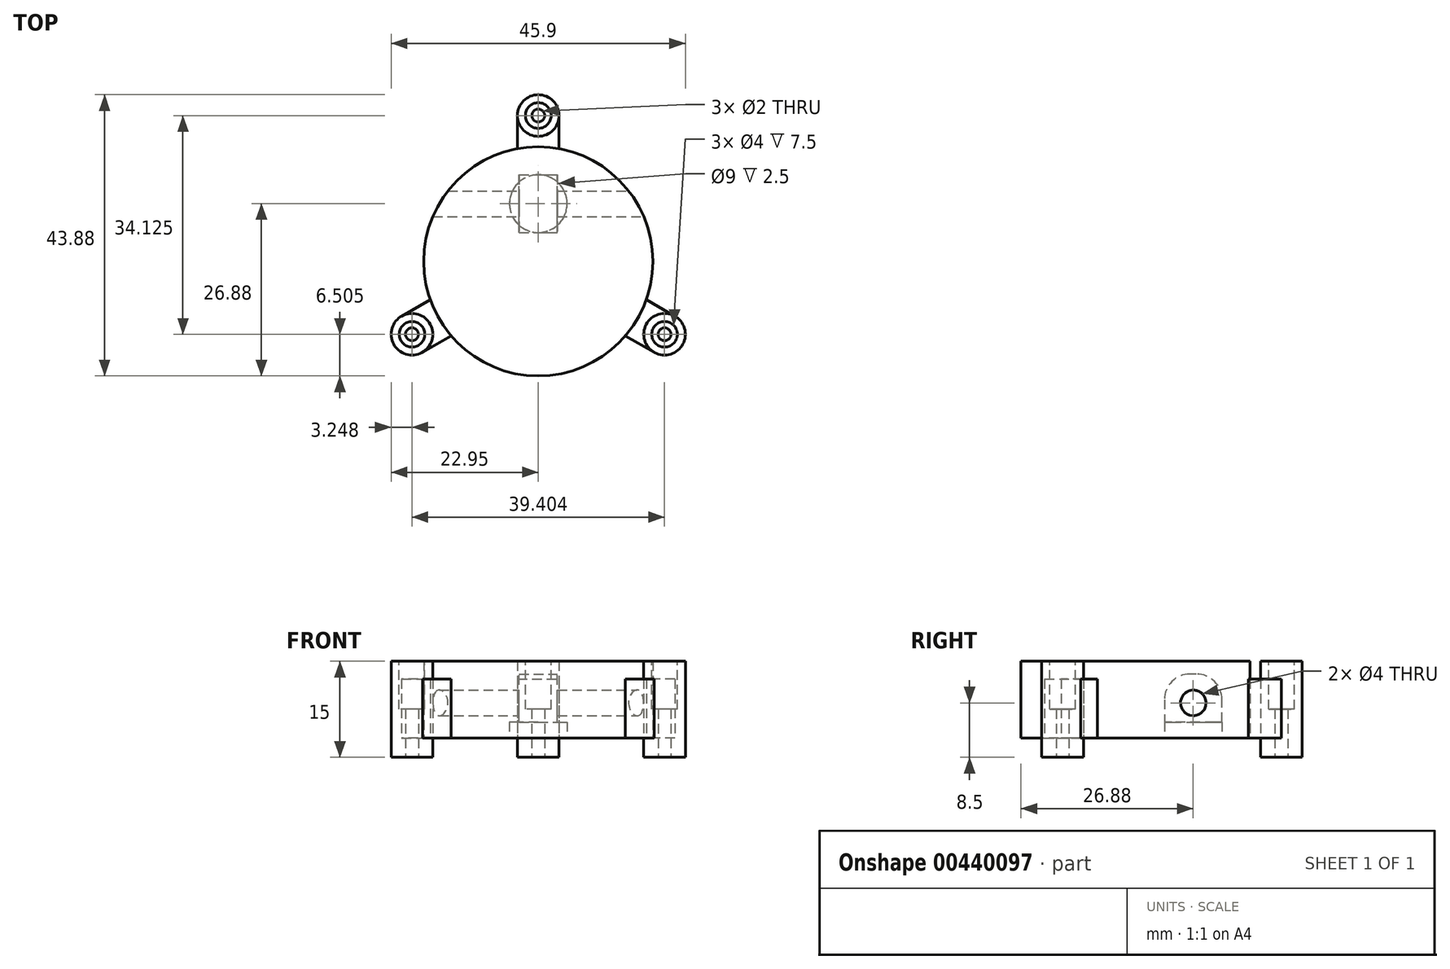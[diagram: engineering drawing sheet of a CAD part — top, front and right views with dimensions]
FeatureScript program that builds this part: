
annotation { "Feature Type Name" : "Feature", "Feature Type Description" : "" }
export const myFeature = defineFeature(function(context is Context, id is Id, definition is map)
    precondition{}
    {
        {
            var Q0;
            Q0=qCreatedBy(makeId("Top.planeOp"),FACE);
            var sketch = newSketch(context, id + "F0", { "sketchPlane" : qUnion([Q0])});
            skLineSegment(sketch, "E0", {"start": v(0, 0) * mm, "end": v(0, 22.75) * mm, "construction": true});
            skLineSegment(sketch, "E1", {"start": v(0, 0) * mm, "end": v(-19.7, -11.37) * mm, "construction": true});
            skLineSegment(sketch, "E2", {"start": v(0, 0) * mm, "end": v(19.7, -11.37) * mm, "construction": true});
            skCircle(sketch, "E3", {"center": v(0, 0) * mm, "radius": 17.88 * mm});
            skCircle(sketch, "E4", {"center": v(0, 22.75) * mm, "radius": 3.25 * mm});
            skCircle(sketch, "E5", {"center": v(-19.7, -11.37) * mm, "radius": 3.25 * mm});
            skCircle(sketch, "E6", {"center": v(19.7, -11.37) * mm, "radius": 3.25 * mm});
            skLineSegment(sketch, "E7", {"start": v(-3.25, 22.75) * mm, "end": v(-3.25, 17.58) * mm});
            skLineSegment(sketch, "E8", {"start": v(3.25, 22.75) * mm, "end": v(3.25, 17.58) * mm});
            skLineSegment(sketch, "E9", {"start": v(-21.33, -8.56) * mm, "end": v(-16.85, -5.97) * mm});
            skLineSegment(sketch, "E10", {"start": v(-18.08, -14.19) * mm, "end": v(-13.6, -11.6) * mm});
            skLineSegment(sketch, "E11", {"start": v(18.08, -14.19) * mm, "end": v(13.6, -11.6) * mm});
            skLineSegment(sketch, "E12", {"start": v(21.33, -8.56) * mm, "end": v(16.85, -5.97) * mm});
            skSolve(sketch);
        }
        {
            var Q0;
            Q0=qCreatedBy(makeId("Front.planeOp"),FACE);
            var sketch = newSketch(context, id + "F1", { "sketchPlane" : qUnion([Q0])});
            skLineSegment(sketch, "E13", {"start": v(0, -12.7) * mm, "end": v(0, 12.7) * mm, "construction": true});
            skSolve(sketch);
        }
        {
            var Q0;
            Q0=sQuery(id+"F1.wireOp",VERTEX,"E13.end");
            var Q1;
            Q1=qCreatedBy(makeId("Top.planeOp"),FACE);
            cPlane(context, id + "F2", {"entities" : qUnion([Q0, Q1]), "cplaneType" : CPlaneType.PLANE_POINT, "offset" : 25.4 * mm, "width" : 152.4 * mm, "height" : 152.4 * mm});
        }
        {
            var Q0;
            Q0=sQuery(id+"F1.wireOp",VERTEX,"E13.start");
            var Q1;
            Q1=qCreatedBy(makeId("Top.planeOp"),FACE);
            cPlane(context, id + "F3", {"entities" : qUnion([Q0, Q1]), "cplaneType" : CPlaneType.PLANE_POINT, "offset" : 25.4 * mm, "oppositeDirection" : true, "width" : 152.4 * mm, "height" : 152.4 * mm});
        }
        {
            var Q0;
            Q0=qCreatedBy(id+"F2.planeOp",FACE);
            var sketch = newSketch(context, id + "F4", { "sketchPlane" : qUnion([Q0])});
            skLineSegment(sketch, "E14", {"start": v(0, 0) * mm, "end": v(0, 22.75) * mm, "construction": true});
            skLineSegment(sketch, "E15", {"start": v(0, 0) * mm, "end": v(-19.7, -11.37) * mm, "construction": true});
            skLineSegment(sketch, "E16", {"start": v(0, 0) * mm, "end": v(19.7, -11.37) * mm, "construction": true});
            skCircle(sketch, "E17", {"center": v(0, 0) * mm, "radius": 17.88 * mm});
            skCircle(sketch, "E18", {"center": v(0, 22.75) * mm, "radius": 3.25 * mm});
            skCircle(sketch, "E19", {"center": v(-19.7, -11.37) * mm, "radius": 3.25 * mm});
            skCircle(sketch, "E20", {"center": v(19.7, -11.37) * mm, "radius": 3.25 * mm});
            skLineSegment(sketch, "E21", {"start": v(-3.25, 22.75) * mm, "end": v(-3.25, 17.58) * mm});
            skLineSegment(sketch, "E22", {"start": v(3.25, 22.75) * mm, "end": v(3.25, 17.58) * mm});
            skLineSegment(sketch, "E23", {"start": v(-21.33, -8.56) * mm, "end": v(-16.85, -5.97) * mm});
            skLineSegment(sketch, "E24", {"start": v(-18.08, -14.19) * mm, "end": v(-13.6, -11.6) * mm});
            skLineSegment(sketch, "E25", {"start": v(18.08, -14.19) * mm, "end": v(13.6, -11.6) * mm});
            skLineSegment(sketch, "E26", {"start": v(21.33, -8.56) * mm, "end": v(16.85, -5.97) * mm});
            skCircle(sketch, "E27", {"center": v(0, 22.75) * mm, "radius": 2 * mm});
            skCircle(sketch, "E28", {"center": v(19.7, -11.37) * mm, "radius": 2 * mm});
            skCircle(sketch, "E29", {"center": v(-19.7, -11.37) * mm, "radius": 2 * mm});
            skSolve(sketch);
        }
        {
            var Q0;
            Q0=qCreatedBy(id+"F3.planeOp",FACE);
            var sketch = newSketch(context, id + "F5", { "sketchPlane" : qUnion([Q0])});
            skLineSegment(sketch, "E30", {"start": v(0, 0) * mm, "end": v(0, 22.75) * mm, "construction": true});
            skLineSegment(sketch, "E31", {"start": v(0, 0) * mm, "end": v(-19.7, -11.37) * mm, "construction": true});
            skLineSegment(sketch, "E32", {"start": v(0, 0) * mm, "end": v(19.7, -11.37) * mm, "construction": true});
            skCircle(sketch, "E33", {"center": v(0, 0) * mm, "radius": 17.88 * mm});
            skCircle(sketch, "E34", {"center": v(0, 22.75) * mm, "radius": 3.25 * mm});
            skCircle(sketch, "E35", {"center": v(-19.7, -11.37) * mm, "radius": 3.25 * mm});
            skCircle(sketch, "E36", {"center": v(19.7, -11.37) * mm, "radius": 3.25 * mm});
            skLineSegment(sketch, "E37", {"start": v(-3.25, 22.75) * mm, "end": v(-3.25, 17.58) * mm});
            skLineSegment(sketch, "E38", {"start": v(3.25, 22.75) * mm, "end": v(3.25, 17.58) * mm});
            skLineSegment(sketch, "E39", {"start": v(-21.33, -8.56) * mm, "end": v(-16.85, -5.97) * mm});
            skLineSegment(sketch, "E40", {"start": v(-18.08, -14.19) * mm, "end": v(-13.6, -11.6) * mm});
            skLineSegment(sketch, "E41", {"start": v(18.08, -14.19) * mm, "end": v(13.6, -11.6) * mm});
            skLineSegment(sketch, "E42", {"start": v(21.33, -8.56) * mm, "end": v(16.85, -5.97) * mm});
            skCircle(sketch, "E43", {"center": v(-19.7, -11.37) * mm, "radius": 2 * mm});
            skCircle(sketch, "E44", {"center": v(19.7, -11.37) * mm, "radius": 2 * mm});
            skCircle(sketch, "E45", {"center": v(0, 22.75) * mm, "radius": 2 * mm});
            skSolve(sketch);
        }
        {
            var Q0;
            {var subQ0=sQuery(id+"F0.wireOp",EDGE,"E4");var subQ1=makeQuery(id+"F0.imprint","INTERSECT",VERTEX,{"derivedFrom":[subQ0,sQuery(id+"F0.wireOp",EDGE,"E7")]});Q0=makeQuery(id+"F0.imprint","IMPRINT",FACE,{"disambiguationData":[TD([[makeQuery(id+"F0.imprint","IMPRINT",EDGE,{"disambiguationData":[TD([[subQ1,1.0]])],"derivedFrom":subQ0}),1.0]])]});}
            var Q1;
            {var subQ0=sQuery(id+"F0.wireOp",EDGE,"E5");var subQ1=makeQuery(id+"F0.imprint","INTERSECT",VERTEX,{"derivedFrom":[subQ0,sQuery(id+"F0.wireOp",EDGE,"E9")]});Q1=makeQuery(id+"F0.imprint","IMPRINT",FACE,{"disambiguationData":[TD([[makeQuery(id+"F0.imprint","IMPRINT",EDGE,{"disambiguationData":[TD([[subQ1,-1.0]])],"derivedFrom":subQ0}),1.0]])]});}
            var Q2;
            {var subQ0=sQuery(id+"F0.wireOp",EDGE,"E6");var subQ1=makeQuery(id+"F0.imprint","INTERSECT",VERTEX,{"derivedFrom":[subQ0,sQuery(id+"F0.wireOp",EDGE,"E11")]});Q2=makeQuery(id+"F0.imprint","IMPRINT",FACE,{"disambiguationData":[TD([[makeQuery(id+"F0.imprint","IMPRINT",EDGE,{"disambiguationData":[TD([[subQ1,1.0]])],"derivedFrom":subQ0}),1.0]])]});}
            extrude(context, id + "F6", {"entities" : qUnion([Q0, Q1, Q2]), "endBound" : BoundingType.SYMMETRIC, "depth" : 15 * mm, "offsetDistance" : 25 * mm});
        }
        {
            var Q0;
            {var subQ0=sQuery(id+"F0.wireOp",EDGE,"E3");var subQ4=makeQuery(id+"F0.imprint","INTERSECT",VERTEX,{"derivedFrom":[subQ0,sQuery(id+"F0.wireOp",EDGE,"E7")]});Q0=makeQuery(id+"F0.imprint","IMPRINT",FACE,{"disambiguationData":[TD([[makeQuery(id+"F0.imprint","IMPRINT",EDGE,{"disambiguationData":[TD([[subQ4,1.0]])],"derivedFrom":subQ0}),1.0]])]});}
            extrude(context, id + "F7", {"entities" : qUnion([Q0]), "endBound" : BoundingType.SYMMETRIC, "depth" : 15 * mm, "offsetDistance" : 25 * mm});
        }
        {
            var Q0;
            {var subQ0=sQuery(id+"F0.wireOp",EDGE,"E7");Q0=makeQuery(id+"F0.imprint","IMPRINT",FACE,{"disambiguationData":[TD([[makeQuery(id+"F0.imprint","IMPRINT",EDGE,{"derivedFrom":subQ0}),1.0]])]});}
            var Q1;
            {var subQ0=sQuery(id+"F0.wireOp",EDGE,"E9");Q1=makeQuery(id+"F0.imprint","IMPRINT",FACE,{"disambiguationData":[TD([[makeQuery(id+"F0.imprint","IMPRINT",EDGE,{"derivedFrom":subQ0}),-1.0]])]});}
            var Q2;
            {var subQ0=sQuery(id+"F0.wireOp",EDGE,"E11");Q2=makeQuery(id+"F0.imprint","IMPRINT",FACE,{"disambiguationData":[TD([[makeQuery(id+"F0.imprint","IMPRINT",EDGE,{"derivedFrom":subQ0}),-1.0]])]});}
            extrude(context, id + "F8", {"entities" : qUnion([Q0, Q1, Q2]), "endBound" : BoundingType.SYMMETRIC, "depth" : 15 * mm, "offsetDistance" : 25 * mm});
        }
        {
            var Q0;
            {var subQ0=sQuery(id+"F4.wireOp",EDGE,"E21");Q0=makeQuery(id+"F4.imprint","IMPRINT",FACE,{"disambiguationData":[TD([[makeQuery(id+"F4.imprint","IMPRINT",EDGE,{"derivedFrom":subQ0}),1.0]])]});}
            var Q1;
            {var subQ0=sQuery(id+"F4.wireOp",EDGE,"E23");Q1=makeQuery(id+"F4.imprint","IMPRINT",FACE,{"disambiguationData":[TD([[makeQuery(id+"F4.imprint","IMPRINT",EDGE,{"derivedFrom":subQ0}),-1.0]])]});}
            var Q2;
            {var subQ0=sQuery(id+"F4.wireOp",EDGE,"E25");Q2=makeQuery(id+"F4.imprint","IMPRINT",FACE,{"disambiguationData":[TD([[makeQuery(id+"F4.imprint","IMPRINT",EDGE,{"derivedFrom":subQ0}),-1.0]])]});}
            extrude(context, id + "F9", {"entities" : qUnion([Q0, Q1, Q2]), "operationType" : NewBodyOperationType.REMOVE, "oppositeDirection" : true, "depth" : 8 * mm, "offsetDistance" : 25 * mm});
        }
        {
            var Q0;
            {var subQ0=sQuery(id+"F5.wireOp",EDGE,"E37");Q0=makeQuery(id+"F5.imprint","IMPRINT",FACE,{"disambiguationData":[TD([[makeQuery(id+"F5.imprint","IMPRINT",EDGE,{"derivedFrom":subQ0}),1.0]])]});}
            var Q1;
            {var subQ0=sQuery(id+"F5.wireOp",EDGE,"E41");Q1=makeQuery(id+"F5.imprint","IMPRINT",FACE,{"disambiguationData":[TD([[makeQuery(id+"F5.imprint","IMPRINT",EDGE,{"derivedFrom":subQ0}),-1.0]])]});}
            var Q2;
            {var subQ0=sQuery(id+"F5.wireOp",EDGE,"E39");Q2=makeQuery(id+"F5.imprint","IMPRINT",FACE,{"disambiguationData":[TD([[makeQuery(id+"F5.imprint","IMPRINT",EDGE,{"derivedFrom":subQ0}),-1.0]])]});}
            extrude(context, id + "F10", {"entities" : qUnion([Q0, Q1, Q2]), "operationType" : NewBodyOperationType.REMOVE, "depth" : 8.2 * mm, "offsetDistance" : 25 * mm});
        }
        {
            var Q0;
            Q0=makeQuery(id+"F6.opExtrude","CAP_FACE",FACE,{"disambiguationData":[OSD([sQuery(id+"F0.wireOp",EDGE,"E4")])],"isStart":true});
            var Q1;
            Q1=makeQuery(id+"F6.opExtrude","CAP_FACE",FACE,{"disambiguationData":[OSD([sQuery(id+"F0.wireOp",EDGE,"E6")])],"isStart":true});
            var Q2;
            Q2=makeQuery(id+"F6.opExtrude","CAP_FACE",FACE,{"disambiguationData":[OSD([sQuery(id+"F0.wireOp",EDGE,"E5")])],"isStart":true});
            shell(context, id + "F11", {"entities" : qUnion([Q0, Q1, Q2]), "thickness" : 2.25 * mm});
        }
        {
            var Q0;
            Q0=makeQuery(id+"F4.imprint","IMPRINT",FACE,{"disambiguationData":[TD([[makeQuery(id+"F4.imprint","IMPRINT",EDGE,{"derivedFrom":sQuery(id+"F4.wireOp",EDGE,"E27")}),1.0]])]});
            var Q1;
            Q1=makeQuery(id+"F4.imprint","IMPRINT",FACE,{"disambiguationData":[TD([[makeQuery(id+"F4.imprint","IMPRINT",EDGE,{"derivedFrom":sQuery(id+"F4.wireOp",EDGE,"E29")}),1.0]])]});
            var Q2;
            Q2=makeQuery(id+"F4.imprint","IMPRINT",FACE,{"disambiguationData":[TD([[makeQuery(id+"F4.imprint","IMPRINT",EDGE,{"derivedFrom":sQuery(id+"F4.wireOp",EDGE,"E28")}),1.0]])]});
            var Q3;
            Q3=sQuery(id+"F5.wireOp",EDGE,"E43");
            var Q4;
            Q4=sQuery(id+"F5.wireOp",EDGE,"E44");
            var Q5;
            Q5=sQuery(id+"F5.wireOp",EDGE,"E45");
            extrude(context, id + "F12", {"entities" : qUnion([Q0, Q1, Q2]), "operationType" : NewBodyOperationType.REMOVE, "surfaceEntities" : qUnion([Q3, Q4, Q5]), "endBound" : BoundingType.SYMMETRIC, "oppositeDirection" : true, "depth" : 25.4 * mm, "offsetDistance" : 25 * mm});
        }
        {
            var Q0;
            Q0=qCreatedBy(makeId("Right.planeOp"),FACE);
            var sketch = newSketch(context, id + "F13", { "sketchPlane" : qUnion([Q0])});
            skLineSegment(sketch, "E46", {"start": v(0, 0) * mm, "end": v(9, 0) * mm, "construction": true});
            skLineSegment(sketch, "E47", {"start": v(9, 0) * mm, "end": v(9, 1) * mm, "construction": true});
            skLineSegment(sketch, "E48", {"start": v(13.5, -3.5) * mm, "end": v(13.5, 1.5) * mm});
            skLineSegment(sketch, "E49", {"start": v(9.5, 5.5) * mm, "end": v(8.5, 5.5) * mm});
            skLineSegment(sketch, "E50", {"start": v(4.5, 1.5) * mm, "end": v(4.5, -3.5) * mm});
            skCircle(sketch, "E51", {"center": v(9, 1) * mm, "radius": 2 * mm});
            skPoint(sketch, "E51.centerSnap0", {"position": v(9, 5.5) * mm});
            skPoint(sketch, "E51.centerSnap1", {"position": v(4.5, 1) * mm});
            skPoint(sketch, "E52.visualSharp", {"position": v(13.5, 5.5) * mm});
            skArc(sketch, "E52.filletArc", {"start": v(13.5, 1.5) * mm, "mid": v(12.33, 4.33) * mm, "end": v(9.5, 5.5) * mm});
            skPoint(sketch, "E53.visualSharp", {"position": v(4.5, 5.5) * mm});
            skArc(sketch, "E53.filletArc", {"start": v(8.5, 5.5) * mm, "mid": v(5.67, 4.33) * mm, "end": v(4.5, 1.5) * mm});
            skLineSegment(sketch, "E54", {"start": v(4.5, -3.5) * mm, "end": v(13.5, -3.5) * mm});
            skLineSegment(sketch, "E55", {"start": v(4.5, -2) * mm, "end": v(13.5, -2) * mm});
            skSolve(sketch);
        }
        {
            var Q0;
            {var subQ0=sQuery(id+"F5.wireOp",EDGE,"E33");var subQ4=makeQuery(id+"F5.imprint","INTERSECT",VERTEX,{"derivedFrom":[subQ0,sQuery(id+"F5.wireOp",EDGE,"E37")]});Q0=makeQuery(id+"F5.imprint","IMPRINT",FACE,{"disambiguationData":[TD([[makeQuery(id+"F5.imprint","IMPRINT",EDGE,{"disambiguationData":[TD([[subQ4,1.0]])],"derivedFrom":subQ0}),1.0]])]});}
            extrude(context, id + "F14", {"entities" : qUnion([Q0]), "operationType" : NewBodyOperationType.REMOVE, "depth" : 8.2 * mm, "offsetDistance" : 25 * mm});
        }
        {
            var Q0;
            Q0=makeQuery(id+"F14.boolean.opBoolean","COPY",FACE,{"derivedFrom":makeQuery(id+"F14.opExtrude","CAP_FACE",FACE,{"disambiguationData":[OSD([sQuery(id+"F5.wireOp",EDGE,"E33")])],"isStart":false})});
            cPlane(context, id + "F15", {"entities" : qUnion([Q0]), "cplaneType" : CPlaneType.OFFSET, "offset" : 0 * mm, "oppositeDirection" : true, "width" : 150 * mm, "height" : 150 * mm});
        }
        {
            var Q0;
            Q0=qCreatedBy(id+"F15.planeOp",FACE);
            var sketch = newSketch(context, id + "F16", { "sketchPlane" : qUnion([Q0])});
            skLineSegment(sketch, "E56", {"start": v(0, 0) * mm, "end": v(0, -9) * mm});
            skCircle(sketch, "E57", {"center": v(0, -9) * mm, "radius": 4.5 * mm});
            skSolve(sketch);
        }
        {
            var Q0;
            Q0 = qSketchRegion(id + "F16", true);
            extrude(context, id + "F17", {"entities" : qUnion([Q0]), "operationType" : NewBodyOperationType.REMOVE, "oppositeDirection" : true, "depth" : 2.5 * mm, "offsetDistance" : 25 * mm});
        }
        {
            var Q0;
            Q0=makeQuery(id+"F13.imprint","IMPRINT",FACE,{"disambiguationData":[TD([[makeQuery(id+"F13.imprint","IMPRINT",EDGE,{"derivedFrom":sQuery(id+"F13.wireOp",EDGE,"E49")}),1.0]])]});
            extrude(context, id + "F18", {"entities" : qUnion([Q0]), "operationType" : NewBodyOperationType.REMOVE, "endBound" : BoundingType.SYMMETRIC, "oppositeDirection" : true, "depth" : 6 * mm, "offsetDistance" : 25 * mm});
        }
        {
            var Q0;
            Q0=makeQuery(id+"F13.imprint","IMPRINT",FACE,{"disambiguationData":[TD([[makeQuery(id+"F13.imprint","IMPRINT",EDGE,{"derivedFrom":sQuery(id+"F13.wireOp",EDGE,"E51")}),1.0]])]});
            var Q1;
            Q1=sQuery(id+"F13.wireOp",EDGE,"E51");
            extrude(context, id + "F19", {"entities" : qUnion([Q0]), "operationType" : NewBodyOperationType.REMOVE, "surfaceEntities" : qUnion([Q1]), "endBound" : BoundingType.SYMMETRIC, "oppositeDirection" : true, "depth" : 43.4 * mm, "offsetDistance" : 25 * mm});
        }
    });
